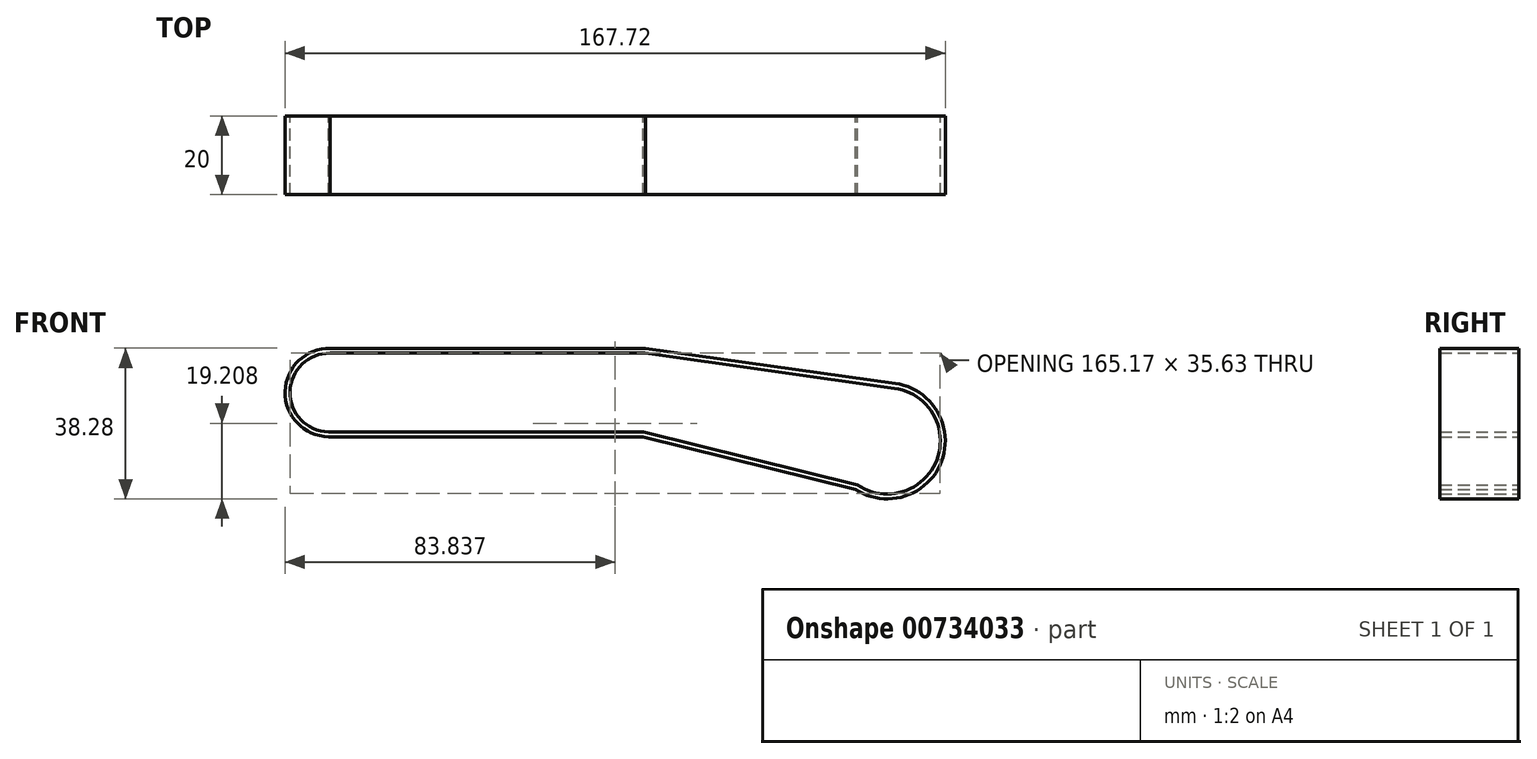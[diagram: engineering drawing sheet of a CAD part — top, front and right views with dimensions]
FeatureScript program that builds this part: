
annotation { "Feature Type Name" : "Feature", "Feature Type Description" : "" }
export const myFeature = defineFeature(function(context is Context, id is Id, definition is map)
    precondition{}
    {
        {
            var Q0;
            Q0=qCreatedBy(makeId("Front.planeOp"),FACE);
            var sketch = newSketch(context, id + "F0", { "sketchPlane" : qUnion([Q0])});
            skLineSegment(sketch, "E0", {"start": v(-46.26, 8.78) * mm, "end": v(33.74, 8.78) * mm});
            skLineSegment(sketch, "E1", {"start": v(-46.7, -11.21) * mm, "end": v(33.3, -11.21) * mm});
            skArc(sketch, "E2", {"start": v(-46.26, 8.78) * mm, "mid": v(-56.48, -1) * mm, "end": v(-46.7, -11.21) * mm});
            skLineSegment(sketch, "E3", {"start": v(33.74, 8.78) * mm, "end": v(97.12, -0.12) * mm});
            skLineSegment(sketch, "E4", {"start": v(33.3, -11.21) * mm, "end": v(87.66, -24.66) * mm});
            skArc(sketch, "E5", {"start": v(87.66, -24.66) * mm, "mid": v(107.83, -18.35) * mm, "end": v(97.12, -0.12) * mm});
            skLineSegment(sketch, "E6.0", {"start": v(34, 10) * mm, "end": v(97.3, 1.11) * mm});
            skLineSegment(sketch, "E7.0", {"start": v(33.14, -12.46) * mm, "end": v(87.14, -25.82) * mm});
            skArc(sketch, "E8.0", {"start": v(87.14, -25.82) * mm, "mid": v(109.04, -18.7) * mm, "end": v(97.3, 1.11) * mm});
            skLineSegment(sketch, "E9.0", {"start": v(-46.25, 10.03) * mm, "end": v(33.74, 10.03) * mm});
            skArc(sketch, "E9.1", {"start": v(-46.25, 10.03) * mm, "mid": v(-57.73, -0.98) * mm, "end": v(-46.72, -12.46) * mm});
            skLineSegment(sketch, "E9.2", {"start": v(-46.72, -12.46) * mm, "end": v(33.14, -12.46) * mm});
            skLineSegment(sketch, "E10", {"start": v(33.74, 10.03) * mm, "end": v(33.83, 10.03) * mm});
            skLineSegment(sketch, "E11", {"start": v(34, 10) * mm, "end": v(33.83, 10.03) * mm});
            skSolve(sketch);
        }
        {
            var Q0;
            Q0=qSketchRegion(id+"F0",true);
            extrude(context, id + "F1", {"entities" : qUnion([Q0]), "depth" : 20 * mm, "offsetDistance" : 25 * mm});
        }
    });
